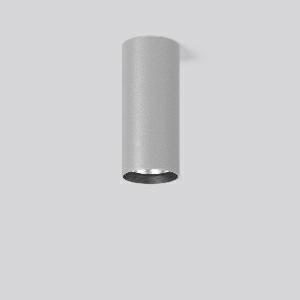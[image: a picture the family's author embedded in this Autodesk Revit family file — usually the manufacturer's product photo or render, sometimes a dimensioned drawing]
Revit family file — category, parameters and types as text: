
# Revit family: heledon_mini_a_931209_004_3_76_2e70
name_source: partatom
category: Lighting Fixtures
units: mm (PartAtom-declared; Revit-internal decimal feet)

## family parameters
Cut with Voids When Loaded = No
Host = Face
Light Source = No
Part Type = Normal
Room Calculation Point = No
Round Connector Dimension = Use Diameter
Shared = No

## types (1)
- HELEDON mini A (1 x LED Modul 935, 3600 lm, 3500)
    Apparent Load = 29 VA
    Approval mark = CE
    CIE Flux Codes = 99 100 100 100 100
    Color Rendering = 92
    Color Temperature = 3500
    Default Elevation = 1800 mm
    Description = Series: HELEDON mini
Cylindrical surface-mounted downlight. Housing: die-cast aluminium, powder-coated. Internal ceiling frame polycarbonate with bayonet mounting. Black plastic ring and recessed LED to prevent glare from the side. Optical assembly with reflector made of MIRO-Silver with 98% total light reflection for outstanding efficiency - can be changed without tools. Best colour rendering index Ra>90. Suitable for Ceiling mounting. Easy installation with a separate ceiling frame with bayonet mounting and plug connection. Driver integrated. Connected via plug-in connector. High quality converter without flickering and stroboscopic effect. The following accessories can be mounted without use of tools: interchangeable lenses, decorative glasses, honeycomb louvre, clear and frosted diffusers, white interchangeable plastic ring. 
Colour: silver
Diameter: 87 mm
Height: 197 mm
Lamp: LED
Socket: without socket
Colour temperature: 3500K
Colour rendering index (CRI): 92
System power: 29 W
Rated luminous flux: 3600 lm
Luminous efficiency: 124 lm/W
Control gear: Converter, dimmable, DALI
Protection class: I
Type of protection: IP 20
    Height = 197 mm
    Lamp = 1 x LED Modul 935
    Lamp Light Flux = 3600 lm
    Lamp count = 1
    Length = 87 mm
    Lifetime = 50000 h
    Luminous efficacy = 124 lm/W
    Manufacturer = RZB
    ModVariant = No
    Model = 931209.004.3.76
    Mounting Place = Ceiling
    Mounting Type = Surface mounted
    Number of Poles = 1
    OnlyDefault = Yes
    Power Factor = 1
    Product Name = HELEDON mini A
    Product group = Surface mounted downlights
    ProductGroupID = 302
    Protection Class = Protection class I
    Protection Degree = IP 20
    RLX_Detail_Level = 1
    RLX_Emergency_Light_Flux = 0 lm
    RLX_Emergency_Type = 0
    RLX_Emergency_Type_DB = No
    RlxData = <blob elided: 107629 chars, md5=e7bacc82>
    Socket = socket
    Standby Power = 0 W
    System Light Flux = 3600 lm
    System Power = 29 W
    Type Comments = Product without accessories
    Type Image = 931188.004.jpg
    URL = http://relux.com
    VarID = ---
    Voltage = 230 V
    Voltage Range = 220-240 V
    Weight = 0.00 kg
    Width = 0 mm  [stored 0 ft]

note: [stored X ft] marks values corroborated as IEEE doubles in the binary element streams (Revit-internal decimal feet)

## geometry (parser evidence)
native form markers: Blend x4, Sweep x10
no freeform markers — native parametric forms only
